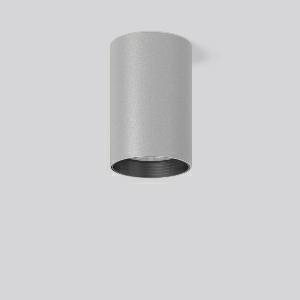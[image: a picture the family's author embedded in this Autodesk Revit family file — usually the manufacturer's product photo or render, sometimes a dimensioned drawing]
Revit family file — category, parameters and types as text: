
# Revit family: heledon_maxi_a_931249_004_2_5b82
name_source: partatom
category: Lighting Fixtures
units: mm (PartAtom-declared; Revit-internal decimal feet)

## family parameters
Cut with Voids When Loaded = No
Host = Face
Light Source = No
Part Type = Normal
Room Calculation Point = No
Round Connector Dimension = Use Diameter
Shared = No

## types (1)
- HELEDON maxi A (1 x LED Modul 927 bakery, 2850 lm, 2700)
    Apparent Load = 33 VA
    Approval mark = CE
    CIE Flux Codes = 96 99 100 100 100
    Color Rendering = 90
    Color Temperature = 2700
    Default Elevation = 1800 mm
    Description = Series: HELEDON maxi
Cylindrical surface-mounted downlight. Housing: die-cast aluminium, powder-coated. Internal ceiling frame polycarbonate with bayonet mounting. Black plastic ring and recessed LED to prevent glare from the side. Optical assembly with lens made of plastic (polycarbonate) for the best homogeneous light distribution - can be changed without tools. Special LED for illumination of pastries included. Suitable for Ceiling mounting. Easy installation with a separate ceiling frame with bayonet mounting and plug connection. Driver integrated. Connected via plug-in connector. High quality converter without flickering and stroboscopic effect. The following accessories can be mounted without use of tools: interchangeable lenses, decorative glasses, honeycomb louvre, clear and frosted diffusers, white interchangeable plastic ring. 
Colour: silver
Diameter: 123 mm
Height: 183 mm
Lamp: LED
Socket: without socket
Colour temperature: bakery
Colour rendering index (CRI): 97
System power: 33 W
Rated luminous flux: 2850 lm
Luminous efficiency: 86 lm/W
Control gear: Regulated power supply
Protection class: I
Type of protection: IP 20
    Height = 183 mm
    Lamp = 1 x LED Modul 927 bakery
    Lamp Light Flux = 2850 lm
    Lamp count = 1
    Length = 123 mm
    Lifetime = 50000 h
    Luminous efficacy = 86 lm/W
    Manufacturer = RZB
    ModVariant = No
    Model = 931249.004.2
    Mounting Place = Ceiling
    Mounting Type = Surface mounted
    Number of Poles = 1
    OnlyDefault = Yes
    Power Factor = 1
    Product Name = HELEDON maxi A
    Product group = Surface mounted downlights
    ProductGroupID = 302
    Protection Class = Protection class I
    Protection Degree = IP 20
    RLX_Detail_Level = 1
    RLX_Emergency_Light_Flux = 0 lm
    RLX_Emergency_Type = 0
    RLX_Emergency_Type_DB = No
    RlxData = <blob elided: 97229 chars, md5=9423c998>
    Socket = socket
    Standby Power = 0 W
    System Light Flux = 2850 lm
    System Power = 33 W
    Type Comments = Product without accessories
    Type Image = 931193.004.jpg
    URL = http://relux.com
    VarID = ---
    Voltage = 230 V
    Voltage Range = 220-240 V
    Weight = 0.00 kg
    Width = 0 mm  [stored 0 ft]

note: [stored X ft] marks values corroborated as IEEE doubles in the binary element streams (Revit-internal decimal feet)

## geometry (parser evidence)
native form markers: Blend x4, Sweep x9
no freeform markers — native parametric forms only
